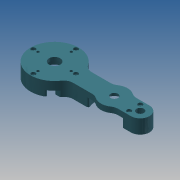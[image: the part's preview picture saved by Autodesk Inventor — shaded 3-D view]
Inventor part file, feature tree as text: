
AUTODESK INVENTOR PART (.ipt)
format: ipt  version: 2013 (Build 170138000, 138)  size: 356,352 bytes
history: native  units: mm
features: extrude x20, sketch x20, fillet x2, projected_geometry x2, mirror x1, pattern_circular x1
ambient origin geometry x8: Origin, YZ Plane, XZ Plane, XY Plane, X Axis, Y Axis, Z Axis, Center Point
bodies: Solid1 (feature_tree)
feature tree (46):
  extrude  "Extrusion1"  Depth=12.5mm
  extrude  "Extrusion2"  Depth=38.0mm TaperAngle=0.0deg
  extrude  "Extrusion3"  Depth=35.0mm
  extrude  "Extrusion4"  Depth=35.0mm TaperAngle=0.0deg
  extrude  "Extrusion5"  Depth=23.0mm TaperAngle=0.0deg
  mirror  "Mirror1"
  extrude  "Extrusion6"  Depth=4.0mm TaperAngle=0.0deg
  extrude  "Extrusion7"  Depth=4.0mm TaperAngle=0.0deg
  extrude  "Extrusion9"  Depth=7.5mm
  extrude  "Extrusion10"  Depth=7.5mm
  extrude  "Extrusion11"  Depth=3.0mm TaperAngle=0.0deg
  extrude  "Extrusion12"  Depth=3.0mm TaperAngle=0.0deg
  extrude  "Extrusion13"  Depth=1.5mm TaperAngle=0.0deg
  extrude  "Extrusion14"  Depth=65.0mm
  extrude  "Extrusion15"  Depth=1.5mm TaperAngle=0.0deg
  extrude  "Extrusion16"  Depth=11.4mm TaperAngle=0.0deg
  extrude  "Extrusion17"  Depth=15.0mm
  extrude  "Extrusion18"  Depth=22.0mm
  extrude  "Extrusion19"  Depth=44.055422mm
  pattern_circular  "Circular Pattern2"  [2 undecoded]
  extrude  "Extrusion20"  Depth=3.5mm
  fillet  "Fillet1"  Radius=7.0mm
  fillet  "Fillet2"  Radius=5.5mm
  extrude  "Extrusion21"  Depth=4.0mm TaperAngle=0.0deg
  sketch  "Sketch1"  dims[d0=115.5mm d2=12.5mm]
  sketch  "Sketch2"  dims[d3=12.0mm d4=38.0mm d5=0.0mm]
  sketch  "Sketch3"  dims[d6=44.563422mm d8=35.0mm]
  sketch  "Sketch4"  dims[d9=10.0mm d10=35.0mm d11=0.0mm]
  sketch  "Sketch5"  dims[d12=50.0mm d14=23.0mm d15=0.0mm]
  sketch  "Sketch6"  dims[d16=21.0mm d19=4.0mm d20=0.0mm]
  projected_geometry  "Projected Loop1"
  sketch  "Sketch7"  dims[d22=7.5mm d23=4.0mm d24=0.0mm]
  sketch  "Sketch9"  dims[d25=3.0mm d27=7.5mm]
  sketch  "Sketch10"  dims[d28=7.5mm d29=7.5mm]
  sketch  "Sketch11"  dims[d30=7.5mm d31=3.0mm d32=0.0mm]
  sketch  "Sketch12"  dims[d33=6.0mm d36=3.0mm d37=0.0mm]
  sketch  "Sketch13"  dims[d43=1.0mm d44=1.5mm d45=0.0mm]
  sketch  "Sketch14"  dims[d46=1.5mm d47=0.0mm d50=65.0mm]
  sketch  "Sketch15"  dims[d51=7.5mm d52=1.5mm d53=0.0mm]
  sketch  "Sketch16"  dims[d54=1.5mm d55=0.0mm d56=11.4mm d57=0.0mm]
  sketch  "Sketch17"  dims[d58=5.0mm d59=0.0mm d60=15.0mm]
  sketch  "Sketch18"  dims[d62=5.0mm d63=0.0mm d64=22.0mm]
  sketch  "Sketch19"  dims[d66=7.0mm d67=0.0mm d68=44.055422mm]
  sketch  "Sketch20"  dims[d71=7.0mm d72=0.0mm]
  sketch  "Sketch21"  dims[d73=28.75mm d74=22.5mm d75=3.5mm d76=7.0mm d77=0.0mm d78=5.5mm d79=4.0mm d80=100.0mm d81=0.0mm d82=0.0mm d83=40.0mm d84=360.0deg d86=6.0mm d88=3.0mm d89=0.0mm d90=2.0mm d91=12.5mm d92=1.0mm d93=1.0mm d94=0.0mm]
  projected_geometry  "Project Cut Edges1"
note: 2 required parameter values undecoded (feature->parameter linkage not recoverable at this tier; creation-order binding heuristic only, values carry confidence <= 0.55)
